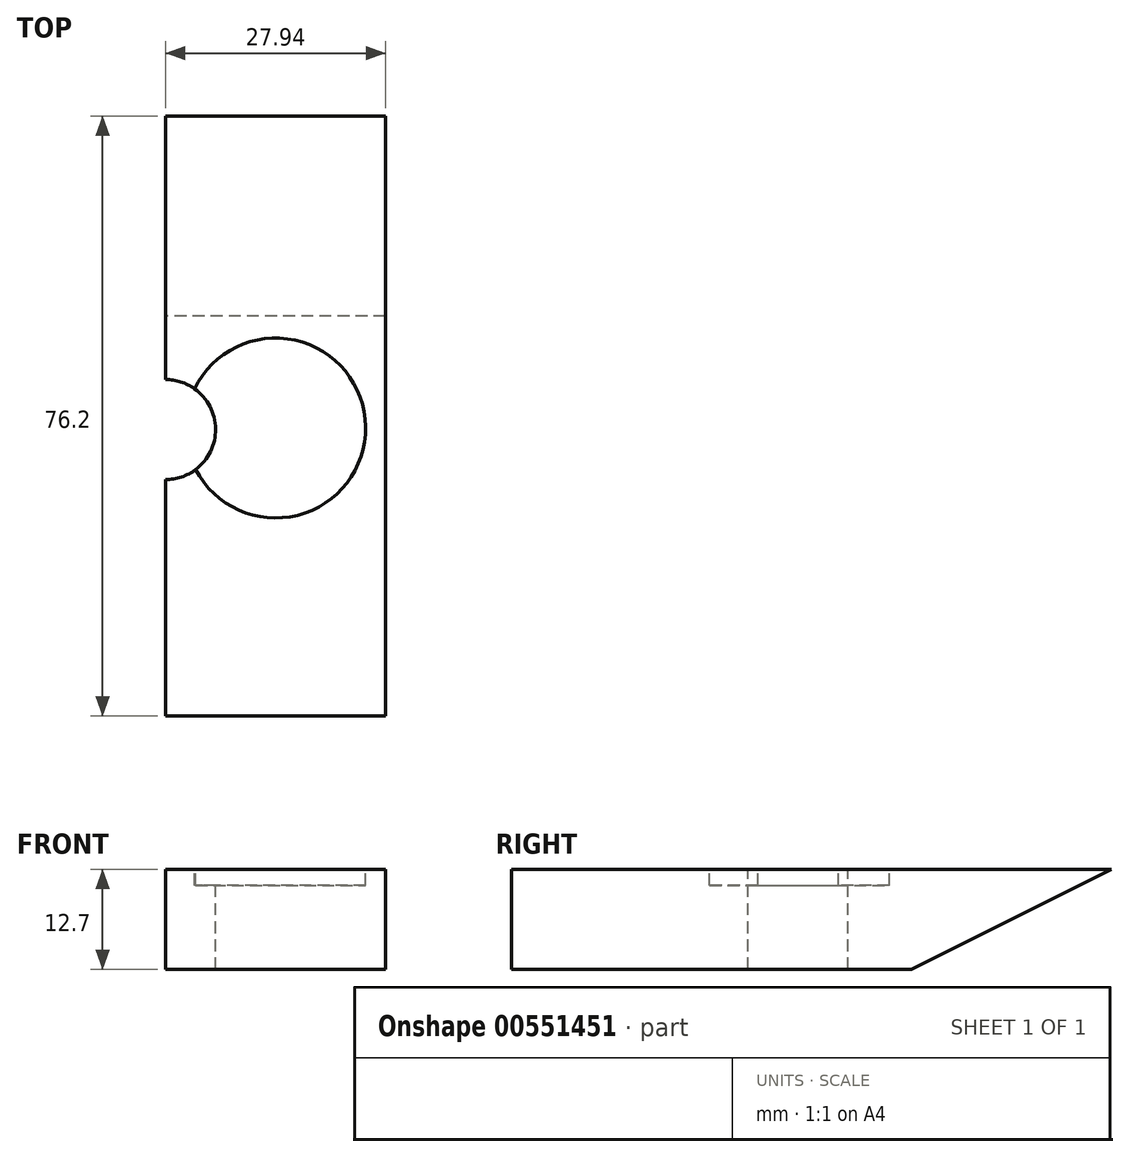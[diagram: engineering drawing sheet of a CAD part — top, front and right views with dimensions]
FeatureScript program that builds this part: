
annotation { "Feature Type Name" : "Feature", "Feature Type Description" : "" }
export const myFeature = defineFeature(function(context is Context, id is Id, definition is map)
    precondition{}
    {
        {
            var Q0;
            Q0=qCreatedBy(makeId("Right.planeOp"),FACE);
            var sketch = newSketch(context, id + "F0", { "sketchPlane" : qUnion([Q0])});
            skLineSegment(sketch, "E0", {"start": v(0, 0) * mm, "end": v(0, 12.7) * mm});
            skLineSegment(sketch, "E1", {"start": v(0, 12.7) * mm, "end": v(76.2, 12.7) * mm});
            skLineSegment(sketch, "E2", {"start": v(76.2, 12.7) * mm, "end": v(50.8, 0) * mm});
            skLineSegment(sketch, "E3", {"start": v(50.8, 0) * mm, "end": v(0, 0) * mm});
            skSolve(sketch);
        }
        {
            var Q0;
            Q0=qSketchRegion(id+"F0",true);
            extrude(context, id + "F1", {"entities" : qUnion([Q0]), "depth" : 27.94 * mm, "offsetDistance" : 25.4 * mm});
        }
        {
            var Q0;
            Q0=makeQuery(id+"F1.opExtrude","SWEPT_FACE",FACE,{"disambiguationData":[OSD([sQuery(id+"F0.wireOp",EDGE,"E1")])]});
            var sketch = newSketch(context, id + "F2", { "sketchPlane" : qUnion([Q0])});
            skCircle(sketch, "E4", {"center": v(13.97, 36.58) * mm, "radius": 11.43 * mm});
            skLineSegment(sketch, "E5", {"start": v(13.97, 76.2) * mm, "end": v(13.97, 48) * mm, "construction": true});
            skPoint(sketch, "E5.endSnap0", {"position": v(13.97, 76.2) * mm});
            skSolve(sketch);
        }
        {
            var Q0;
            Q0 = qSketchRegion(id + "F2", true);
            extrude(context, id + "F3", {"entities" : qUnion([Q0]), "operationType" : NewBodyOperationType.REMOVE, "oppositeDirection" : true, "depth" : 2 * mm, "offsetDistance" : 25.4 * mm});
        }
        {
            var Q0;
            Q0=makeQuery(id+"F1.opExtrude","SWEPT_FACE",FACE,{"disambiguationData":[OSD([sQuery(id+"F0.wireOp",EDGE,"E1")])]});
            var sketch = newSketch(context, id + "F4", { "sketchPlane" : qUnion([Q0])});
            skLineSegment(sketch, "E6", {"start": v(0, 0) * mm, "end": v(0, 36.38) * mm, "construction": true});
            skLineSegment(sketch, "E7", {"start": v(0, 36.38) * mm, "end": v(6.35, 36.38) * mm, "construction": true});
            skCircle(sketch, "E8", {"center": v(0, 36.38) * mm, "radius": 6.35 * mm});
            skSolve(sketch);
        }
        {
            var Q0;
            Q0 = qSketchRegion(id + "F4", true);
            extrude(context, id + "F5", {"entities" : qUnion([Q0]), "operationType" : NewBodyOperationType.REMOVE, "oppositeDirection" : true, "depth" : 25.4 * mm, "offsetDistance" : 25.4 * mm});
        }
    });
